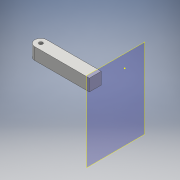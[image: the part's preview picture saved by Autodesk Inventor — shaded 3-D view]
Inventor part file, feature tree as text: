
AUTODESK INVENTOR PART (.ipt)
format: ipt  version: 2016 (Build 200138000, 138)  size: 147,456 bytes
history: native  units: mm
features: sketch x7, extrude x5, fillet x1, hole x1, plane x1, split x1
ambient origin geometry x8: Origin, YZ Plane, XZ Plane, XY Plane, X Axis, Y Axis, Z Axis, Center Point
bodies: Solid1 (feature_tree)
feature tree (16):
  extrude  "Extrusion1"  Depth=60.0mm
  extrude  "Extrusion2"  Depth=41.0mm
  extrude  "Extrusion3"  Depth=10.0mm
  extrude  "Extrusion5"  Depth=15.0mm TaperAngle=0.0deg
  extrude  "Extrusion6"  Depth=9.871mm TaperAngle=0.0deg
  sketch  "Sketch7"  dims[d19=50.0mm d20=0.0mm d21=5.0mm]
  fillet  "Fillet1"  Radius=9.871mm
  hole  "Hole1"  [1 undecoded]
  plane  "Work Plane1"
  split  "Split1"
  sketch  "Sketch1"  dims[d0=15.0mm d1=60.0mm]
  sketch  "Sketch2"  dims[d2=3.0mm d3=0.0mm d4=41.0mm]
  sketch  "Sketch3"  dims[d5=19.0mm d6=0.0mm d7=10.0mm]
  sketch  "Sketch5"  dims[d8=21.64mm d9=15.0mm d10=0.0mm]
  sketch  "Sketch6"  dims[d15=45.0deg d16=15.0mm d17=0.0mm d18=9.871mm]
  sketch  "Sketch8"  dims[d22=3.0mm d23=6.0mm d24=4.0mm d25=2.0mm d26=90.0deg d27=8.0mm d28=20.594885mm d29=0.0mm]
note: 1 required parameter value undecoded (feature->parameter linkage not recoverable at this tier; creation-order binding heuristic only, values carry confidence <= 0.55)
